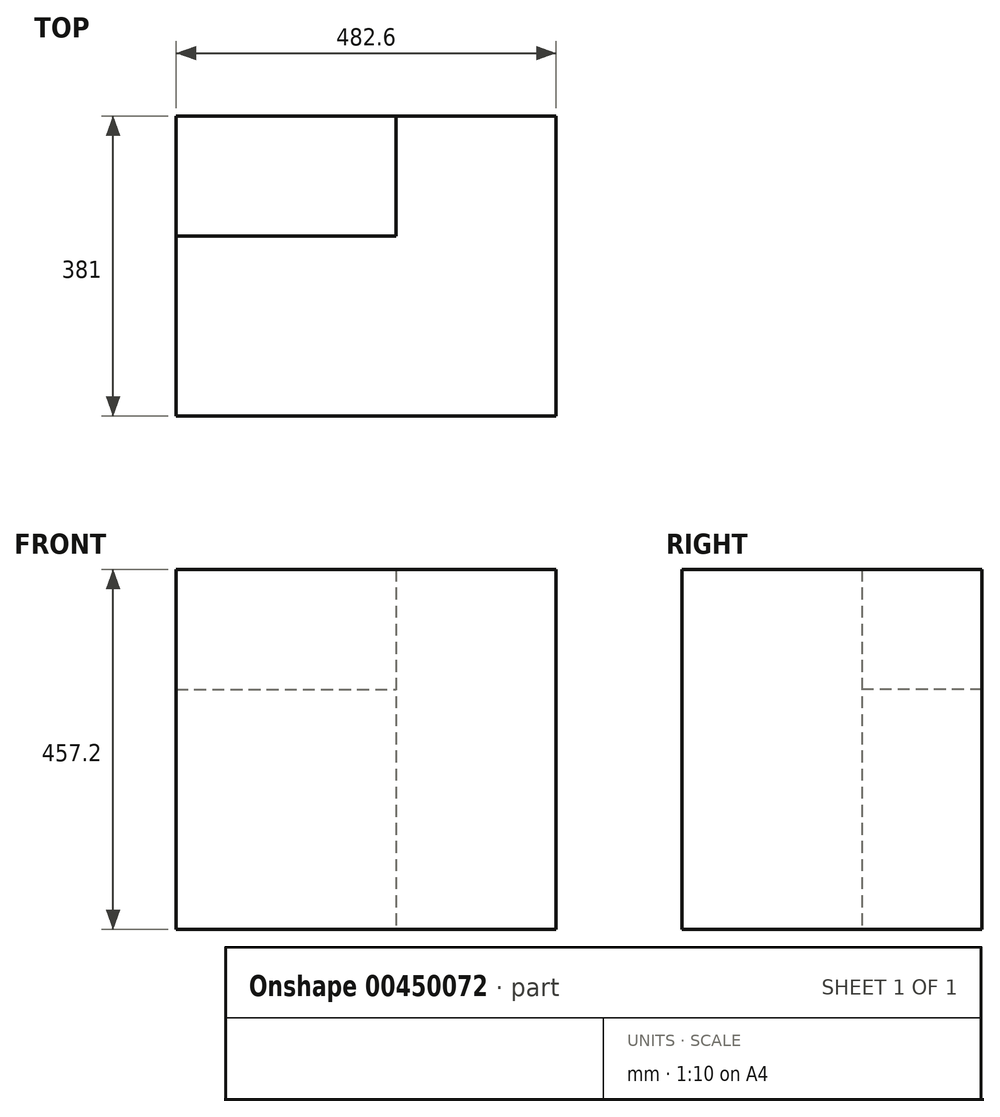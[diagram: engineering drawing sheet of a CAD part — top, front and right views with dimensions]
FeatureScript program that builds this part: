
annotation { "Feature Type Name" : "Feature", "Feature Type Description" : "" }
export const myFeature = defineFeature(function(context is Context, id is Id, definition is map)
    precondition{}
    {
        {
            var Q0;
            Q0=qCreatedBy(makeId("Top.planeOp"),FACE);
            var sketch = newSketch(context, id + "F0", { "sketchPlane" : qUnion([Q0])});
            skLineSegment(sketch, "E0.bottom", {"start": v(-241.3, 114.3) * mm, "end": v(241.3, 114.3) * mm});
            skLineSegment(sketch, "E0.top", {"start": v(-241.3, -114.3) * mm, "end": v(241.3, -114.3) * mm});
            skLineSegment(sketch, "E0.left", {"start": v(-241.3, 114.3) * mm, "end": v(-241.3, -114.3) * mm});
            skLineSegment(sketch, "E0.right", {"start": v(241.3, 114.3) * mm, "end": v(241.3, -114.3) * mm});
            skPoint(sketch, "E0.middle", {"position": v(0, 0) * mm});
            skLineSegment(sketch, "E1.top", {"start": v(241.3, 266.7) * mm, "end": v(38.1, 266.7) * mm});
            skLineSegment(sketch, "E1.left", {"start": v(241.3, 114.3) * mm, "end": v(241.3, 266.7) * mm});
            skLineSegment(sketch, "E1.right", {"start": v(38.1, 114.3) * mm, "end": v(38.1, 266.7) * mm});
            skSolve(sketch);
        }
        {
            var Q0;
            Q0=makeQuery(id+"F0.imprint","IMPRINT",FACE,{"disambiguationData":[TD([[makeQuery(id+"F0.imprint","IMPRINT",EDGE,{"derivedFrom":sQuery(id+"F0.wireOp",EDGE,"E0.bottom")}),-1.0]])]});
            var Q1;
            Q1=makeQuery(id+"F0.imprint","IMPRINT",FACE,{"disambiguationData":[TD([[makeQuery(id+"F0.imprint","IMPRINT",EDGE,{"derivedFrom":sQuery(id+"F0.wireOp",EDGE,"E1.top")}),1.0]])]});
            extrude(context, id + "F1", {"entities" : qUnion([Q0, Q1]), "depth" : 457.2 * mm});
        }
        {
            var Q0;
            Q0=makeQuery(id+"F1.opExtrude","SWEPT_FACE",FACE,{"disambiguationData":[OSD([sQuery(id+"F0.wireOp",EDGE,"E0.bottom")])]});
            var sketch = newSketch(context, id + "F2", { "sketchPlane" : qUnion([Q0])});
            skLineSegment(sketch, "E2.bottom", {"start": v(241.3, 457.2) * mm, "end": v(-38.1, 457.2) * mm});
            skLineSegment(sketch, "E2.top", {"start": v(241.3, 304.8) * mm, "end": v(-38.1, 304.8) * mm});
            skLineSegment(sketch, "E2.left", {"start": v(241.3, 457.2) * mm, "end": v(241.3, 304.8) * mm});
            skLineSegment(sketch, "E2.right", {"start": v(-38.1, 457.2) * mm, "end": v(-38.1, 304.8) * mm});
            skSolve(sketch);
        }
        {
            var Q0;
            Q0=makeQuery(id+"F2.imprint","IMPRINT",FACE,{"disambiguationData":[TD([[makeQuery(id+"F2.imprint","IMPRINT",EDGE,{"derivedFrom":sQuery(id+"F2.wireOp",EDGE,"E2.bottom")}),1.0]])]});
            extrude(context, id + "F3", {"entities" : qUnion([Q0]), "depth" : 152.4 * mm});
        }
    });
